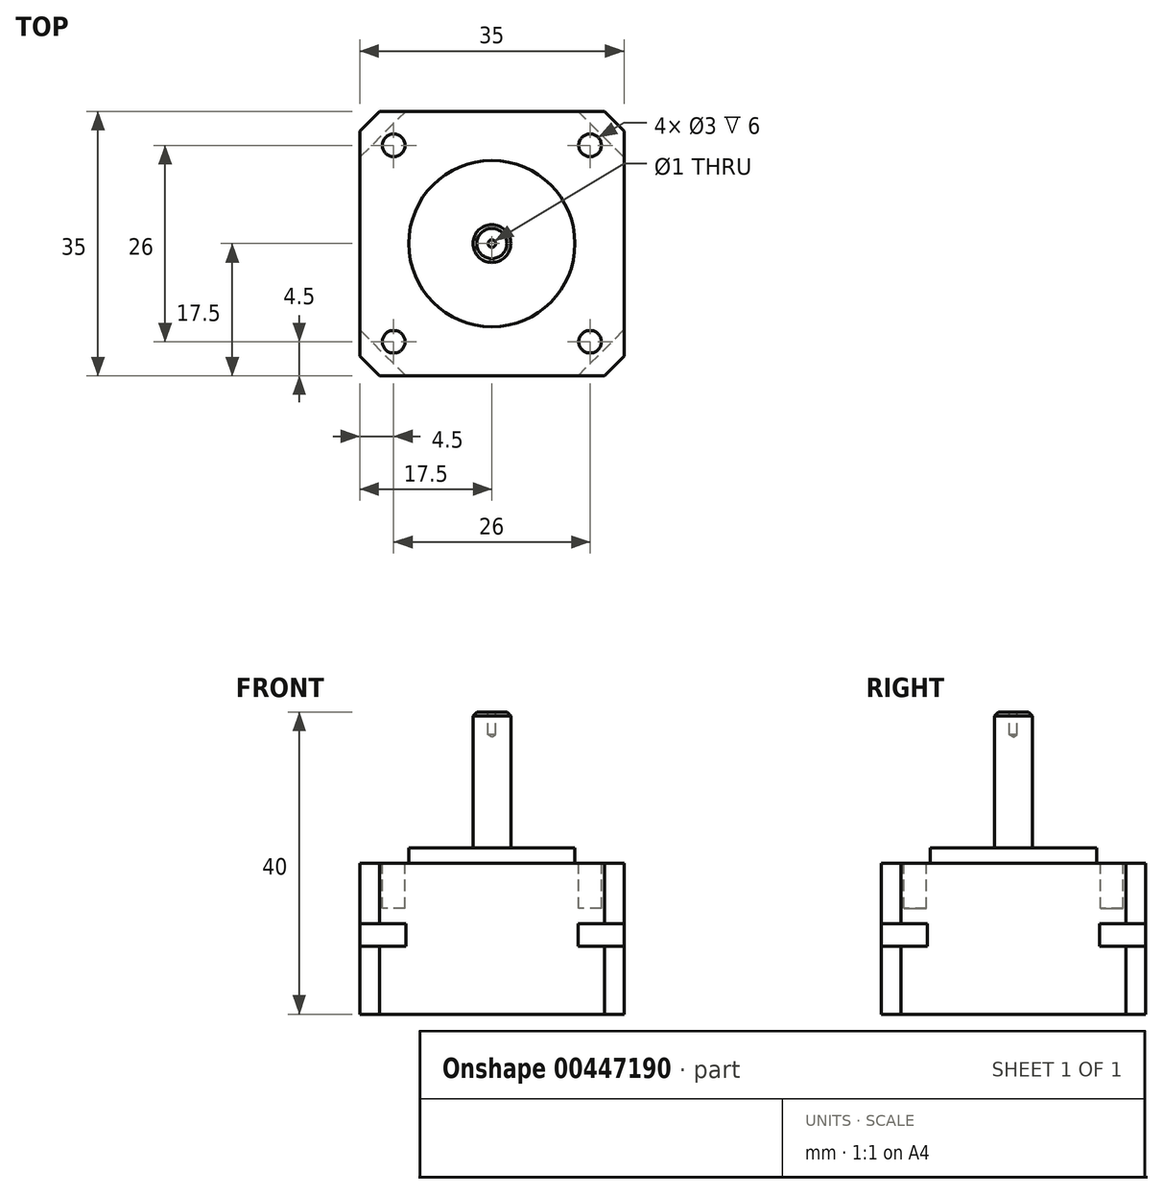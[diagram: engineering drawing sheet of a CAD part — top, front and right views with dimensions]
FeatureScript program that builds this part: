
annotation { "Feature Type Name" : "Feature", "Feature Type Description" : "" }
export const myFeature = defineFeature(function(context is Context, id is Id, definition is map)
    precondition{}
    {
        {
            var Q0;
            Q0=qCreatedBy(makeId("Top.planeOp"),FACE);
            var sketch = newSketch(context, id + "F0", { "sketchPlane" : qUnion([Q0])});
            skLineSegment(sketch, "E0.rect.bottom", {"start": v(-17.5, 17.5) * mm, "end": v(17.5, 17.5) * mm});
            skLineSegment(sketch, "E0.rect.top", {"start": v(-17.5, -17.5) * mm, "end": v(17.5, -17.5) * mm});
            skLineSegment(sketch, "E0.rect.left", {"start": v(-17.5, 17.5) * mm, "end": v(-17.5, -17.5) * mm});
            skLineSegment(sketch, "E0.rect.right", {"start": v(17.5, 17.5) * mm, "end": v(17.5, -17.5) * mm});
            skPoint(sketch, "E0.rect.middle", {"position": v(0, 0) * mm});
            skLineSegment(sketch, "E1", {"start": v(-17.5, 17.5) * mm, "end": v(17.5, -17.5) * mm, "construction": true});
            skSolve(sketch);
        }
        {
            var Q0;
            Q0=qSketchRegion(id+"F0",true);
            extrude(context, id + "F1", {"entities" : qUnion([Q0]), "endBound" : BoundingType.SYMMETRIC, "depth" : 3 * mm});
        }
        {
            var Q0;
            Q0=makeQuery(id+"F1.opExtrude","SWEPT_EDGE",EDGE,{"disambiguationData":[OSD([sQuery(id+"F0.wireOp",EDGE,"E0.rect.top"),sQuery(id+"F0.wireOp",EDGE,"E0.rect.left")])]});
            var Q1;
            Q1=makeQuery(id+"F1.opExtrude","SWEPT_EDGE",EDGE,{"disambiguationData":[OSD([sQuery(id+"F0.wireOp",EDGE,"E0.rect.top"),sQuery(id+"F0.wireOp",EDGE,"E0.rect.right")])]});
            var Q2;
            Q2=makeQuery(id+"F1.opExtrude","SWEPT_EDGE",EDGE,{"disambiguationData":[OSD([sQuery(id+"F0.wireOp",EDGE,"E0.rect.bottom"),sQuery(id+"F0.wireOp",EDGE,"E0.rect.right")])]});
            var Q3;
            Q3=makeQuery(id+"F1.opExtrude","SWEPT_EDGE",EDGE,{"disambiguationData":[OSD([sQuery(id+"F0.wireOp",EDGE,"E0.rect.bottom"),sQuery(id+"F0.wireOp",EDGE,"E0.rect.left")])]});
            chamfer(context, id + "F2", {"entities" : qUnion([Q0, Q1, Q2, Q3]), "width" : 6.1 * mm, "tangentPropagation" : true});
        }
        {
            var Q0;
            Q0=makeQuery(id+"F1.opExtrude","CAP_FACE",FACE,{"disambiguationData":[OSD([sQuery(id+"F0.wireOp",EDGE,"E0.rect.bottom"),sQuery(id+"F0.wireOp",EDGE,"E0.rect.top"),sQuery(id+"F0.wireOp",EDGE,"E0.rect.left"),sQuery(id+"F0.wireOp",EDGE,"E0.rect.right")])],"isStart":false});
            var sketch = newSketch(context, id + "F3", { "sketchPlane" : qUnion([Q0])});
            skLineSegment(sketch, "E2.0", {"start": v(-17.5, 17.5) * mm, "end": v(17.5, 17.5) * mm});
            skLineSegment(sketch, "E2.1", {"start": v(-17.5, -17.5) * mm, "end": v(17.5, -17.5) * mm});
            skLineSegment(sketch, "E2.2", {"start": v(-17.5, 17.5) * mm, "end": v(-17.5, -17.5) * mm});
            skLineSegment(sketch, "E2.3", {"start": v(17.5, 17.5) * mm, "end": v(17.5, -17.5) * mm});
            skPoint(sketch, "E2.4", {"position": v(0, 0) * mm});
            skSolve(sketch);
        }
        {
            var Q0;
            Q0=qSketchRegion(id+"F3",true);
            extrude(context, id + "F4", {"entities" : qUnion([Q0]), "operationType" : NewBodyOperationType.ADD, "depth" : 8 * mm});
        }
        {
            var Q0;
            Q0=makeQuery(id+"F4.opExtrude","SWEPT_EDGE",EDGE,{"disambiguationData":[OSD([sQuery(id+"F3.wireOp",EDGE,"E2.1"),sQuery(id+"F3.wireOp",EDGE,"E2.2")])]});
            var Q1;
            Q1=makeQuery(id+"F4.opExtrude","SWEPT_EDGE",EDGE,{"disambiguationData":[OSD([sQuery(id+"F3.wireOp",EDGE,"E2.1"),sQuery(id+"F3.wireOp",EDGE,"E2.3")])]});
            var Q2;
            Q2=makeQuery(id+"F4.opExtrude","SWEPT_EDGE",EDGE,{"disambiguationData":[OSD([sQuery(id+"F3.wireOp",EDGE,"E2.0"),sQuery(id+"F3.wireOp",EDGE,"E2.3")])]});
            var Q3;
            Q3=makeQuery(id+"F4.opExtrude","SWEPT_EDGE",EDGE,{"disambiguationData":[OSD([sQuery(id+"F3.wireOp",EDGE,"E2.0"),sQuery(id+"F3.wireOp",EDGE,"E2.2")])]});
            chamfer(context, id + "F5", {"entities" : qUnion([Q0, Q1, Q2, Q3]), "width" : 2.6 * mm, "tangentPropagation" : true});
        }
        {
            var Q0;
            Q0=makeQuery(id+"F1.opExtrude","CAP_FACE",FACE,{"disambiguationData":[OSD([sQuery(id+"F0.wireOp",EDGE,"E0.rect.bottom"),sQuery(id+"F0.wireOp",EDGE,"E0.rect.top"),sQuery(id+"F0.wireOp",EDGE,"E0.rect.left"),sQuery(id+"F0.wireOp",EDGE,"E0.rect.right")])],"isStart":true});
            var sketch = newSketch(context, id + "F6", { "sketchPlane" : qUnion([Q0])});
            skLineSegment(sketch, "E3.0.0", {"start": v(14.9, -17.5) * mm, "end": v(-14.9, -17.5) * mm});
            skLineSegment(sketch, "E3.0.1", {"start": v(-14.9, -17.5) * mm, "end": v(-17.5, -14.9) * mm});
            skLineSegment(sketch, "E3.0.2", {"start": v(-17.5, -14.9) * mm, "end": v(-17.5, 14.9) * mm});
            skLineSegment(sketch, "E3.0.3", {"start": v(-17.5, 14.9) * mm, "end": v(-14.9, 17.5) * mm});
            skLineSegment(sketch, "E3.0.4", {"start": v(-14.9, 17.5) * mm, "end": v(14.9, 17.5) * mm});
            skLineSegment(sketch, "E3.0.5", {"start": v(14.9, 17.5) * mm, "end": v(17.5, 14.9) * mm});
            skLineSegment(sketch, "E3.0.6", {"start": v(17.5, 14.9) * mm, "end": v(17.5, -14.9) * mm});
            skLineSegment(sketch, "E3.0.7", {"start": v(17.5, -14.9) * mm, "end": v(14.9, -17.5) * mm});
            skSolve(sketch);
        }
        {
            var Q0;
            Q0=qSketchRegion(id+"F6",true);
            extrude(context, id + "F7", {"entities" : qUnion([Q0]), "operationType" : NewBodyOperationType.ADD, "depth" : 9 * mm});
        }
        {
            var Q0;
            Q0=makeQuery(id+"F4.opExtrude","CAP_FACE",FACE,{"disambiguationData":[OSD([sQuery(id+"F3.wireOp",EDGE,"E2.0"),sQuery(id+"F3.wireOp",EDGE,"E2.1"),sQuery(id+"F3.wireOp",EDGE,"E2.2"),sQuery(id+"F3.wireOp",EDGE,"E2.3")])],"isStart":false});
            var sketch = newSketch(context, id + "F8", { "sketchPlane" : qUnion([Q0])});
            skCircle(sketch, "E4", {"center": v(0, 0) * mm, "radius": 11 * mm});
            skSolve(sketch);
        }
        {
            var Q0;
            Q0=qSketchRegion(id+"F8",true);
            extrude(context, id + "F9", {"entities" : qUnion([Q0]), "operationType" : NewBodyOperationType.ADD, "depth" : 2 * mm});
        }
        {
            var Q0;
            Q0=makeQuery(id+"F9.opExtrude","CAP_FACE",FACE,{"disambiguationData":[OSD([sQuery(id+"F8.wireOp",EDGE,"E4")])],"isStart":false});
            var sketch = newSketch(context, id + "F10", { "sketchPlane" : qUnion([Q0])});
            skCircle(sketch, "E5", {"center": v(0, 0) * mm, "radius": 2.5 * mm});
            skSolve(sketch);
        }
        {
            var Q0;
            Q0=makeQuery(id+"F10.imprint","IMPRINT",FACE,{"disambiguationData":[TD([[makeQuery(id+"F10.imprint","IMPRINT",EDGE,{"derivedFrom":sQuery(id+"F10.wireOp",EDGE,"E5")}),1.0]])]});
            extrude(context, id + "F11", {"entities" : qUnion([Q0]), "operationType" : NewBodyOperationType.ADD, "depth" : 18 * mm});
        }
        {
            var Q0;
            Q0=makeQuery(id+"F4.opExtrude","CAP_FACE",FACE,{"disambiguationData":[OSD([sQuery(id+"F3.wireOp",EDGE,"E2.0"),sQuery(id+"F3.wireOp",EDGE,"E2.1"),sQuery(id+"F3.wireOp",EDGE,"E2.2"),sQuery(id+"F3.wireOp",EDGE,"E2.3")])],"isStart":false});
            var sketch = newSketch(context, id + "F12", { "sketchPlane" : qUnion([Q0])});
            skCircle(sketch, "E6", {"center": v(-13, 13) * mm, "radius": 1.5 * mm});
            skCircle(sketch, "E7.MirrorC", {"center": v(13, 13) * mm, "radius": 1.5 * mm});
            skCircle(sketch, "E8.MirrorC", {"center": v(-13, -13) * mm, "radius": 1.5 * mm});
            skCircle(sketch, "E9.MirrorC", {"center": v(13, -13) * mm, "radius": 1.5 * mm});
            skLineSegment(sketch, "E10", {"start": v(-13, 13) * mm, "end": v(13, -13) * mm, "construction": true});
            skLineSegment(sketch, "E11.rect.bottom", {"start": v(-13, 13) * mm, "end": v(13, 13) * mm, "construction": true});
            skLineSegment(sketch, "E11.rect.top", {"start": v(-13, -13) * mm, "end": v(13, -13) * mm, "construction": true});
            skLineSegment(sketch, "E11.rect.left", {"start": v(-13, 13) * mm, "end": v(-13, -13) * mm, "construction": true});
            skLineSegment(sketch, "E11.rect.right", {"start": v(13, 13) * mm, "end": v(13, -13) * mm, "construction": true});
            skPoint(sketch, "E11.rect.middle", {"position": v(0, 0) * mm});
            skSolve(sketch);
        }
        {
            var Q0;
            Q0=qSketchRegion(id+"F12",true);
            extrude(context, id + "F13", {"entities" : qUnion([Q0]), "operationType" : NewBodyOperationType.REMOVE, "oppositeDirection" : true, "depth" : 6 * mm});
        }
        {
            var Q0;
            Q0=makeQuery(id+"F11.opExtrude","CAP_FACE",FACE,{"disambiguationData":[OSD([sQuery(id+"F10.wireOp",EDGE,"E5")])],"isStart":false});
            chamfer(context, id + "F14", {"entities" : qUnion([Q0]), "width" : 0.5 * mm, "tangentPropagation" : true});
        }
        {
            var Q0;
            Q0=makeQuery(id+"F11.opExtrude","CAP_FACE",FACE,{"disambiguationData":[OSD([sQuery(id+"F10.wireOp",EDGE,"E5")])],"isStart":false});
            var sketch = newSketch(context, id + "F15", { "sketchPlane" : qUnion([Q0])});
            skPoint(sketch, "E12", {"position": v(0, 0) * mm});
            skSolve(sketch);
        }
        {
            var Q0;
            Q0=sQuery(id+"F15.wireOp",VERTEX,"E12");
            var Q1;
            Q1=makeQuery(id+"F1.opExtrude","SWEPT_BODY",BODY,{"disambiguationData":[OSD([sQuery(id+"F0.wireOp",EDGE,"E0.rect.bottom"),sQuery(id+"F0.wireOp",EDGE,"E0.rect.top"),sQuery(id+"F0.wireOp",EDGE,"E0.rect.left"),sQuery(id+"F0.wireOp",EDGE,"E0.rect.right")])]});
            hole(context, id + "F16", {"style" : HoleStyle.SIMPLE, "holeDiameter" : 1 * mm, "endStyle" : HoleEndStyle.BLIND, "holeDepth" : 3 * mm, "locations" : qUnion([Q0]), "scope" : qUnion([Q1])});
        }
    });
